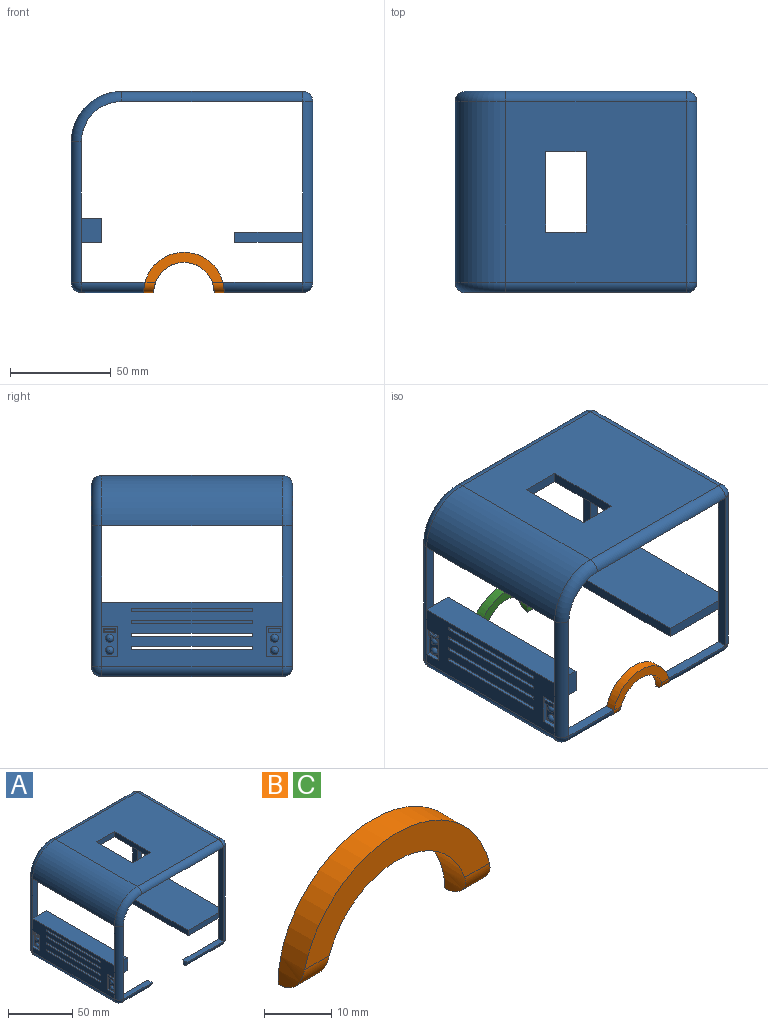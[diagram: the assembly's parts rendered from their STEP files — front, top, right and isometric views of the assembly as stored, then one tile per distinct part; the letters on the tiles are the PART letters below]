
ASSEMBLY  parts=3 mates=2
PART A: 108 faces, bbox 122.1x100x102.1 mm
  f0: plane 90x90mm, normal (0,0,1), area 7300mm2, adj f16,f21,f25,f31,f104,f105,f106,f107
  f1: plane 100x95mm, normal (0,0,-1), area 8650mm2, adj f2,f21,f25,f31,f71,f95,f101,f103
  f2: plane 90x5mm, normal (-1,0,0), area 450mm2, adj f1,f26,f37,f93,f94,f101
  f3: plane 90x33.77mm, normal (0,0,-1), area 3038.9mm2, adj f73,f93,f97,f100
  f4: plane 12x10mm, normal (0,-1,0), area 120mm2, adj f12,f13,f39,f74
  f5: plane 12x10mm, normal (0,1,0), area 120mm2, adj f12,f13,f39,f74
  f6: plane 90x4.68mm, normal (0,0,-1), area 421.2mm2, adj f68,f69,f72,f95
  f7: cylinder r=20mm len=5mm, axis (0,1,0), area 19.9mm2, adj f17,f38,f98
  f8: plane 31.64x5mm, normal (0,-1,0), area 156.1mm2, adj f12,f15,f27,f99
  f9: cylinder r=20mm len=5mm, axis (0,1,0), area 19.9mm2, adj f10,f32,f96
  f10: plane 31.64x5mm, normal (0,1,0), area 156.1mm2, adj f9,f12,f32,f96
  f11: plane 90x32mm, normal (-1,0,0), area 2280mm2, adj f13,f28,f33,f36,f40,f42,f43,f45
  f12: plane 100x75mm, normal (1,0,0), area 2770mm2, adj f4,f5,f8,f10,f28,f33,f36,f39
  f13: plane 90x15mm, normal (0,0,1), area 1350mm2, adj f4,f5,f11,f68,f69,f74
  f14: cylinder r=20mm len=5mm, axis (0,1,0), area 19.9mm2, adj f20,f37,f94
  f15: cylinder r=20mm len=5mm, axis (0,1,0), area 19.9mm2, adj f8,f27,f99
  f16: cylinder r=25mm len=90mm, axis (0,-1,0), area 3534.3mm2, adj f0,f24,f34,f70
  f17: cylinder r=5mm len=39.64mm, axis (1,0,0), area 307.4mm2, adj f7,f18,f38,f98
  f18: sphere r=5mm, area 39.3mm2, adj f17,f19,f38
  f19: cylinder r=5mm len=90mm, axis (0,0,1), area 706.9mm2, adj f18,f22,f38,f71,f103
  f20: cylinder r=5mm len=39.64mm, axis (-1,0,0), area 307.4mm2, adj f14,f23,f37,f94
  f21: cylinder r=5mm len=90mm, axis (-1,0,0), area 706.9mm2, adj f0,f1,f22,f24
  f22: sphere r=5mm, area 39.3mm2, adj f19,f21,f25
  f23: sphere r=5mm, area 39.3mm2, adj f20,f26,f37
  f24: torus R=20mm, axis (0,-1,0), area 286mm2, adj f16,f21,f28,f95
  f25: cylinder r=5mm len=90mm, axis (0,1,0), area 706.9mm2, adj f0,f1,f22,f29
  f26: cylinder r=5mm len=90mm, axis (0,0,-1), area 706.9mm2, adj f2,f23,f29,f37,f101
  f27: cylinder r=5mm len=31.64mm, axis (1,0,0), area 244.6mm2, adj f8,f15,f30,f99
  f28: cylinder r=5mm len=70mm, axis (0,0,-1), area 549.8mm2, adj f11,f12,f24,f30,f41,f68
  f29: sphere r=5mm, area 39.3mm2, adj f25,f26,f31
  f30: sphere r=5mm, area 39.3mm2, adj f27,f28,f33
  f31: cylinder r=5mm len=90mm, axis (1,0,0), area 706.9mm2, adj f0,f1,f29,f34
  f32: cylinder r=5mm len=31.64mm, axis (-1,0,0), area 244.6mm2, adj f9,f10,f35,f96
  f33: cylinder r=5mm len=90mm, axis (0,1,0), area 706.9mm2, adj f11,f12,f30,f35
  f34: torus R=20mm, axis (0,-1,0), area 286mm2, adj f16,f31,f36,f95
  f35: sphere r=5mm, area 39.3mm2, adj f32,f33,f36
  f36: cylinder r=5mm len=70mm, axis (0,0,1), area 549.8mm2, adj f11,f12,f34,f35,f48,f69
  f37: plane 44.64x30mm, normal (0,1,0), area 321.1mm2, adj f2,f14,f20,f23,f26,f73,f94
  f38: plane 44.64x30mm, normal (0,-1,0), area 321.1mm2, adj f7,f17,f18,f19,f71,f73,f98
  f39: plane 90x10mm, normal (0,0,-1), area 900mm2, adj f4,f5,f12,f74
  f40: plane 8x2mm, normal (0,0,-1), area 16mm2, adj f11,f41,f43,f44
  f41: plane 15x2mm, normal (0,-1,0), area 30mm2, adj f28,f40,f42,f44
  f42: plane 8x2mm, normal (0,0,1), area 16mm2, adj f11,f41,f43,f44
  f43: plane 15x2mm, normal (0,1,0), area 30mm2, adj f11,f40,f42,f44
  f44: plane 15x8mm, normal (-1,0,0), area 82.9mm2, adj f40,f41,f42,f43,f50,f51,f52,f53
  f45: plane 8x2mm, normal (0,0,-1), area 16mm2, adj f11,f46,f48,f49
  f46: plane 15x2mm, normal (0,-1,0), area 30mm2, adj f11,f45,f47,f49
  f47: plane 8x2mm, normal (0,0,1), area 16mm2, adj f11,f46,f48,f49
  f48: plane 15x2mm, normal (0,1,0), area 30mm2, adj f36,f45,f47,f49
  f49: plane 15x8mm, normal (-1,0,0), area 82.9mm2, adj f45,f46,f47,f48,f55,f56,f57,f58
  f50: plane 6x1.5mm, normal (0,0,1), area 9mm2, adj f44,f51,f53,f63
  f51: plane 2x1.5mm, normal (0,1,0), area 3mm2, adj f44,f50,f52,f65
  f52: plane 6x1.5mm, normal (0,0,-1), area 9mm2, adj f44,f51,f53,f64
  f53: plane 2x1.5mm, normal (0,-1,0), area 3mm2, adj f44,f50,f52,f62
  f54: plane 5x1mm, normal (-1,0,0), area 5mm2, adj f62,f63,f64,f65
  f55: plane 6x2mm, normal (0,0,1), area 12mm2, adj f49,f56,f58,f59
  f56: plane 2x2mm, normal (0,1,0), area 4mm2, adj f49,f55,f57,f59
  f57: plane 6x2mm, normal (0,0,-1), area 12mm2, adj f49,f56,f58,f59
  f58: plane 2x2mm, normal (0,-1,0), area 4mm2, adj f49,f55,f57,f59
  f59: plane 6x2mm, normal (-1,0,0), area 12mm2, adj f55,f56,f57,f58
  f60: sphere r=2mm, area 25.1mm2, adj f44
  f61: sphere r=2mm, area 25.1mm2, adj f44
  f62: cylinder r=0.5mm len=2mm, axis (0,0,-1), area 1.3mm2, adj f53,f54,f63,f64
  f63: cylinder r=0.5mm len=6mm, axis (0,-1,0), area 4.4mm2, adj f50,f54,f62,f65
  f64: cylinder r=0.5mm len=6mm, axis (0,1,0), area 4.4mm2, adj f52,f54,f62,f65
  f65: cylinder r=0.5mm len=2mm, axis (0,0,1), area 1.3mm2, adj f51,f54,f63,f64
  f66: sphere r=2mm, area 25.1mm2, adj f49
  f67: sphere r=2mm, area 25.1mm2, adj f49
  f68: plane 48x7.68mm, normal (0,-1,0), area 218.7mm2, adj f6,f12,f13,f28,f70,f72,f95
  f69: plane 48x7.68mm, normal (0,1,0), area 218.7mm2, adj f6,f12,f13,f36,f70,f72,f95
  f70: plane 90x3mm, normal (0,0,-1), area 270mm2, adj f16,f68,f69,f72
  f71: plane 90x5mm, normal (-1,0,0), area 450mm2, adj f1,f19,f38,f97,f98,f103
  f72: plane 90x10mm, normal (1,0,0), area 900mm2, adj f6,f68,f69,f70
  f73: cylinder r=5mm len=90mm, axis (0,1,0), area 706.9mm2, adj f3,f37,f38,f102
  f74: plane 90x12mm, normal (1,0,0), area 1080mm2, adj f4,f5,f13,f39
  f75: plane 60x5mm, normal (0,0,-1), area 300mm2, adj f11,f12,f76,f78
  f76: plane 5x1.5mm, normal (0,-1,0), area 7.5mm2, adj f11,f12,f75,f77
  f77: plane 60x5mm, normal (0,0,1), area 300mm2, adj f11,f12,f76,f78
  f78: plane 5x1.5mm, normal (0,1,0), area 7.5mm2, adj f11,f12,f75,f77
  f79: plane 60x5mm, normal (0,0,-1), area 300mm2, adj f11,f12,f80,f82
  f80: plane 5x1.5mm, normal (0,-1,0), area 7.5mm2, adj f11,f12,f79,f81
  f81: plane 60x5mm, normal (0,0,1), area 300mm2, adj f11,f12,f80,f82
  f82: plane 5x1.5mm, normal (0,1,0), area 7.5mm2, adj f11,f12,f79,f81
  f83: plane 60x5mm, normal (0,0,-1), area 300mm2, adj f11,f84,f86,f87
  f84: plane 5x1.5mm, normal (0,-1,0), area 7.5mm2, adj f11,f83,f85,f87
  f85: plane 60x5mm, normal (0,0,1), area 300mm2, adj f11,f84,f86,f87
  f86: plane 5x1.5mm, normal (0,1,0), area 7.5mm2, adj f11,f83,f85,f87
  f87: plane 60x1.5mm, normal (-1,0,0), area 90mm2, adj f83,f84,f85,f86
  f88: plane 60x5mm, normal (0,0,-1), area 300mm2, adj f11,f89,f91,f92
  f89: plane 5x1.5mm, normal (0,-1,0), area 7.5mm2, adj f11,f88,f90,f92
  f90: plane 60x5mm, normal (0,0,1), area 300mm2, adj f11,f89,f91,f92
  f91: plane 5x1.5mm, normal (0,1,0), area 7.5mm2, adj f11,f88,f90,f92
  f92: plane 60x1.5mm, normal (-1,0,0), area 90mm2, adj f88,f89,f90,f91
  f93: plane 33.77x5mm, normal (0,-1,0), area 168.8mm2, adj f2,f3,f100,f102
  f94: plane 39.64x5mm, normal (0,0,1), area 198.2mm2, adj f2,f14,f20,f37
  f95: cylinder r=20mm len=100mm, axis (0,-1,0), area 2199.1mm2, adj f1,f6,f12,f24,f34,f68,f69
  f96: plane 31.64x5mm, normal (0,0,1), area 158.2mm2, adj f9,f10,f12,f32
  f97: plane 33.77x5mm, normal (0,1,0), area 168.8mm2, adj f3,f71,f100,f102
  f98: plane 39.64x5mm, normal (0,0,1), area 198.2mm2, adj f7,f17,f38,f71
  f99: plane 31.64x5mm, normal (0,0,1), area 158.2mm2, adj f8,f12,f15,f27
  f100: plane 90x5mm, normal (-1,0,0), area 450mm2, adj f3,f93,f97,f102
  f101: plane 65x5mm, normal (0,1,0), area 325mm2, adj f1,f2,f26,f102
  f102: plane 90x38.77mm, normal (0,0,1), area 3488.9mm2, adj f73,f93,f97,f100,f101,f103
  f103: plane 65x5mm, normal (0,-1,0), area 325mm2, adj f1,f19,f71,f102
  f104: plane 40x5mm, normal (1,0,0), area 200mm2, adj f0,f1,f105,f107
  f105: plane 20x5mm, normal (0,1,0), area 100mm2, adj f0,f1,f104,f106
  f106: plane 40x5mm, normal (-1,0,0), area 200mm2, adj f0,f1,f105,f107
  f107: plane 20x5mm, normal (0,-1,0), area 100mm2, adj f0,f1,f104,f106
PART B: 8 faces, bbox 40x5x20 mm
  f0: cylinder r=15mm len=30mm, axis (0,1,0), area 225.7mm2, adj f1,f3,f4,f5,f6,f7
  f1: plane 5x0.2mm, normal (0,0,-1), area 1mm2, adj f0,f2,f5,f6
  f2: cylinder r=20mm len=40mm, axis (0,1,0), area 304.2mm2, adj f1,f3,f4,f5,f6,f7
  f3: plane 5x0.2mm, normal (0,0,-1), area 1mm2, adj f0,f2,f5,f7
  f4: plane 38.83x15.2mm, normal (0,-1,0), area 226.3mm2, adj f0,f2,f6,f7
  f5: plane 40x20mm, normal (0,1,0), area 274.9mm2, adj f0,f1,f2,f3
  f6: cylinder r=4.8mm len=5.79mm, axis (-1,0,0), area 38mm2, adj f0,f1,f2,f4
  f7: cylinder r=4.8mm len=5.79mm, axis (-1,0,0), area 38mm2, adj f0,f2,f3,f4
PART C: same geometry as B
PLACE A t=(-90.83,23.54,-33.38)mm
PLACE B t=(-55.55,-71.46,-45.05)mm
PLACE C rot(axis=(0,0,1),180deg) t=(-55.55,18.54,-45.05)mm
MATE fastened C.f5 <-> A.f38  axis (0,-1,0) through (-35.55,18.54,-45.05)mm
MATE fastened B.f5 <-> A.f10  axis (0,1,0) through (-75.55,-71.46,-45.05)mm
